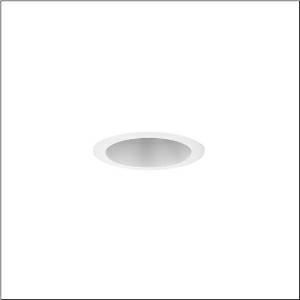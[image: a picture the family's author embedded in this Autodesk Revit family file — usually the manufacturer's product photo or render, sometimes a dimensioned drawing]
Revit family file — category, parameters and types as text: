
# Revit family: lunis_31-l_51dn15me31b
name_source: partatom
category: Lighting Fixtures
units: mm (PartAtom-declared; Revit-internal decimal feet)

## family parameters
Cut with Voids When Loaded = No
Host = Face
Light Source = No
Part Type = Normal
Room Calculation Point = No
Round Connector Dimension = Use Diameter
Shared = No

## types (1)
- --- (1 x LED, 1600 lm, 12 W, 3000K)
    Apparent Load = 12 VA
    CIE Flux Codes = 93 98 100 100 100
    Color Rendering = 80
    Color Temperature = 3000K
    Default Elevation = 1800 mm
    Description = Lunis 31-L, downlight, light control with reflector, light emission: direct distribution, LED rated luminous flux: 1.600lm, light colour: 830, mains connection: 220..240V, AC/DC, 0/50..60Hz, housing, of aluminium, white, protection rating (complete): IP20, protection rating (on room side): IP54, insulation class (complete): insulation class II (safety insulation), certification: CE, ENEC, packaging unit: 1 piece
    Height = 0 mm  [stored 0 ft]
    Lamp = 1 x LED
    Lamp Light Flux = 1600 lm
    Lamp Power = 12 W
    Lamp count = 1
    Length = 188 mm  [stored 0.616798 ft]
    Luminous efficacy = 133 lm/W
    Manufacturer = Siteco
    ModVariant = No
    Model = 51DN15ME31B
    Mounting Place = Ceiling
    Mounting Type = Recessed
    Number of Poles = 1
    OnlyDefault = Yes
    Power Factor = 1
    Product Name = Lunis 31-L
    Product group = downlight
    ProductGroupID = 401
    Protection Class = Protection class II
    Protection Degree = IP 20
    RLX_Detail_Level = 1
    RLX_Emergency_Light_Flux = 0 lm
    RLX_Emergency_Type = 0
    RLX_Emergency_Type_DB = No
    RlxData = <blob elided: 22233 chars, md5=041bb596>
    Socket = socket
    Standby Power = 0 W
    System Light Flux = 1600 lm
    System Power = 12 W
    Type Comments = individual setting: luminous flux: 100 % | (OFF | ON) | 300 mA
    Type Image = l_1345911.jpg
    URL = http://relux.com
    VarID = @adj_029681
    Voltage = 0 V
    Weight = 0.00 kg
    Width = 0 mm  [stored 0 ft]

note: [stored X ft] marks values corroborated as IEEE doubles in the binary element streams (Revit-internal decimal feet)

## geometry (parser evidence)
native form markers: Blend x4, Sweep x9
no freeform markers — native parametric forms only
